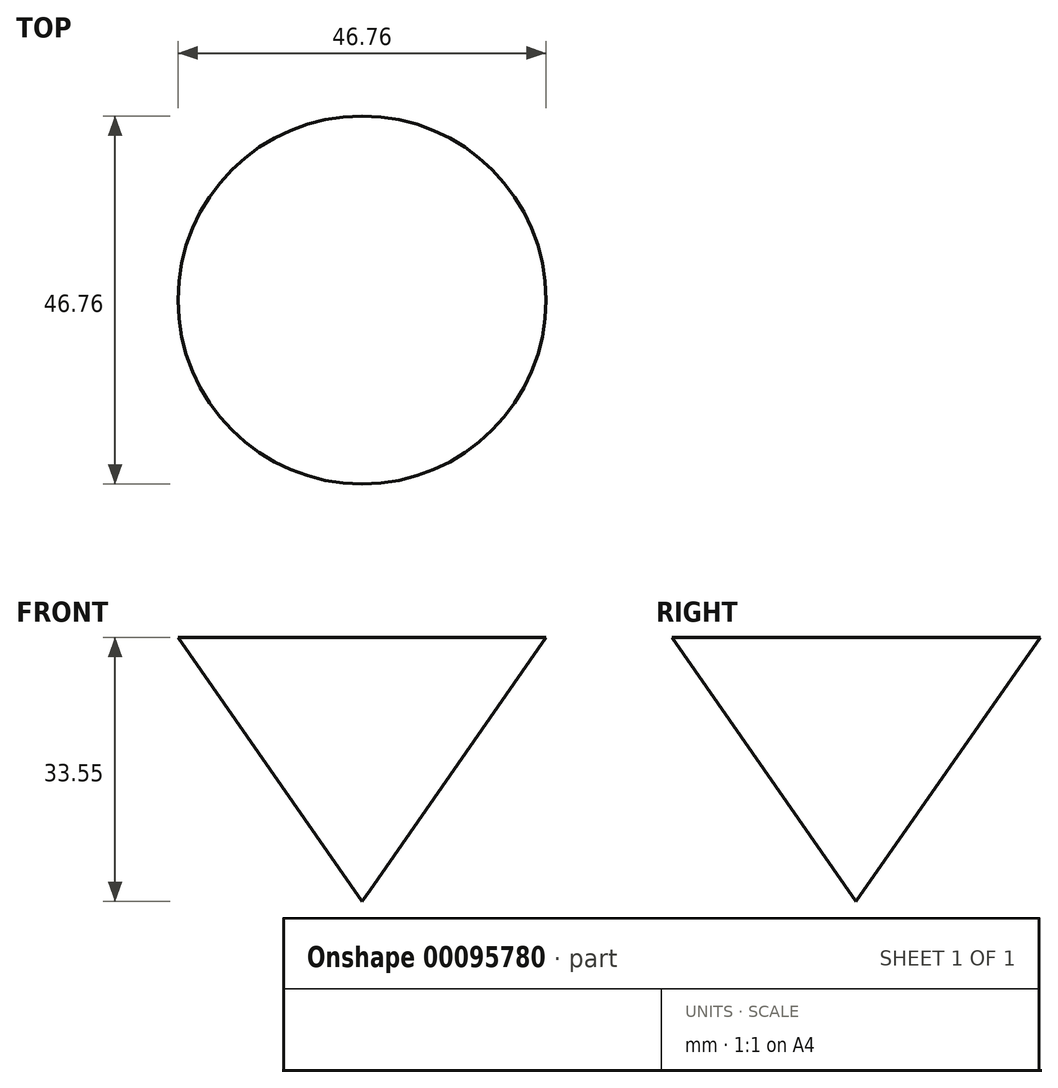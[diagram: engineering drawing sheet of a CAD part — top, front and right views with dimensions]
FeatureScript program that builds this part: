
annotation { "Feature Type Name" : "Feature", "Feature Type Description" : "" }
export const myFeature = defineFeature(function(context is Context, id is Id, definition is map)
    precondition{}
    {
        {
            var Q0;
            Q0=qCreatedBy(makeId("Right.planeOp"),FACE);
            var sketch = newSketch(context, id + "F0", { "sketchPlane" : qUnion([Q0])});
            skLineSegment(sketch, "E0", {"start": v(0, 0) * mm, "end": v(23.38, 0) * mm});
            skLineSegment(sketch, "E1", {"start": v(23.38, 0) * mm, "end": v(0, -33.55) * mm});
            skLineSegment(sketch, "E2", {"start": v(0, -33.55) * mm, "end": v(0, 0) * mm});
            skSolve(sketch);
        }
        {
            var Q0;
            Q0=makeQuery(id+"F0.imprint","IMPRINT",FACE,{"disambiguationData":[TD([[makeQuery(id+"F0.imprint","IMPRINT",EDGE,{"derivedFrom":sQuery(id+"F0.wireOp",EDGE,"E0")}),-1.0]])]});
            var Q1;
            Q1=sQuery(id+"F0.wireOp",EDGE,"E2");
            revolve(context, id + "F1", {"entities" : qUnion([Q0]), "axis" : qUnion([Q1]), "revolveType" : RevolveType.FULL});
        }
        {
            var Q0;
            Q0=qCreatedBy(makeId("Top.planeOp"),FACE);
            var sketch = newSketch(context, id + "F2", { "sketchPlane" : qUnion([Q0])});
            skCircle(sketch, "E3.cCircle", {"center": v(0, 0) * mm, "radius": 22.93 * mm, "construction": true});
            skLineSegment(sketch, "E3.0", {"start": v(0, 22.93) * mm, "end": v(16.21, 16.21) * mm});
            skLineSegment(sketch, "E3.1", {"start": v(16.21, 16.21) * mm, "end": v(22.93, 0) * mm});
            skLineSegment(sketch, "E3.2", {"start": v(22.93, 0) * mm, "end": v(16.21, -16.21) * mm});
            skLineSegment(sketch, "E3.3", {"start": v(16.21, -16.21) * mm, "end": v(0, -22.93) * mm});
            skLineSegment(sketch, "E3.4", {"start": v(0, -22.93) * mm, "end": v(-16.21, -16.21) * mm});
            skLineSegment(sketch, "E3.5", {"start": v(-16.21, -16.21) * mm, "end": v(-22.93, 0) * mm});
            skLineSegment(sketch, "E3.6", {"start": v(-22.93, 0) * mm, "end": v(-16.21, 16.21) * mm});
            skLineSegment(sketch, "E3.7", {"start": v(-16.21, 16.21) * mm, "end": v(0, 22.93) * mm});
            skSolve(sketch);
        }
    });
